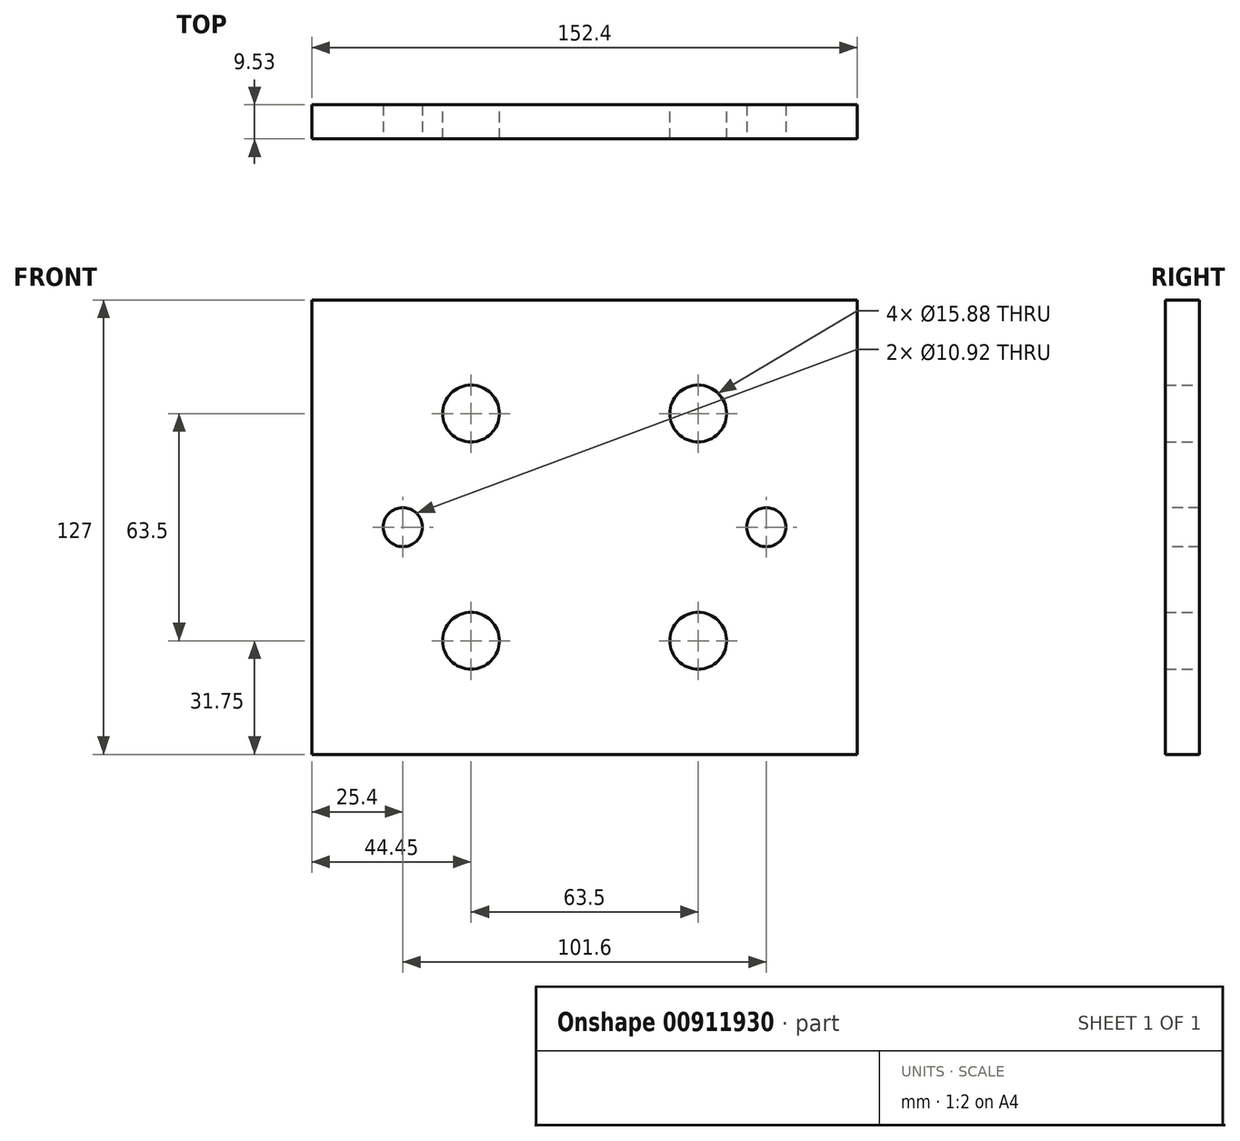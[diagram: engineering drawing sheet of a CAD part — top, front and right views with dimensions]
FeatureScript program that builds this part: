
annotation { "Feature Type Name" : "Feature", "Feature Type Description" : "" }
export const myFeature = defineFeature(function(context is Context, id is Id, definition is map)
    precondition{}
    {
        {
            var Q0;
            Q0=qCreatedBy(makeId("Front.planeOp"),FACE);
            var sketch = newSketch(context, id + "F0", { "sketchPlane" : qUnion([Q0])});
            skLineSegment(sketch, "E0.bottom", {"start": v(0, 0) * mm, "end": v(152.4, 0) * mm});
            skLineSegment(sketch, "E0.top", {"start": v(0, 127) * mm, "end": v(152.4, 127) * mm});
            skLineSegment(sketch, "E0.left", {"start": v(0, 0) * mm, "end": v(0, 127) * mm});
            skLineSegment(sketch, "E0.right", {"start": v(152.4, 0) * mm, "end": v(152.4, 127) * mm});
            skCircle(sketch, "E1", {"center": v(44.45, 31.75) * mm, "radius": 7.94 * mm});
            skCircle(sketch, "E2", {"center": v(107.95, 31.75) * mm, "radius": 7.94 * mm});
            skCircle(sketch, "E3", {"center": v(107.95, 95.25) * mm, "radius": 7.94 * mm});
            skCircle(sketch, "E4", {"center": v(44.45, 95.25) * mm, "radius": 7.94 * mm});
            skSolve(sketch);
        }
        {
            var Q0;
            Q0=makeQuery(id+"F0.imprint","IMPRINT",FACE,{"disambiguationData":[TD([[makeQuery(id+"F0.imprint","IMPRINT",EDGE,{"derivedFrom":sQuery(id+"F0.wireOp",EDGE,"E0.bottom")}),1.0]])]});
            extrude(context, id + "F1", {"entities" : qUnion([Q0]), "depth" : 9.52 * mm, "offsetDistance" : 25.4 * mm});
        }
        {
            var Q0;
            Q0=makeQuery(id+"F1.opExtrude","CAP_FACE",FACE,{"disambiguationData":[OSD([sQuery(id+"F0.wireOp",EDGE,"E0.bottom"),sQuery(id+"F0.wireOp",EDGE,"E0.top"),sQuery(id+"F0.wireOp",EDGE,"E0.left"),sQuery(id+"F0.wireOp",EDGE,"E0.right"),sQuery(id+"F0.wireOp",EDGE,"E1"),sQuery(id+"F0.wireOp",EDGE,"E2"),sQuery(id+"F0.wireOp",EDGE,"E3"),sQuery(id+"F0.wireOp",EDGE,"E4")])],"isStart":false});
            var sketch = newSketch(context, id + "F2", { "sketchPlane" : qUnion([Q0])});
            skCircle(sketch, "E5", {"center": v(25.4, 63.5) * mm, "radius": 5.46 * mm});
            skCircle(sketch, "E6", {"center": v(127, 63.5) * mm, "radius": 5.46 * mm});
            skSolve(sketch);
        }
        {
            var Q0;
            Q0=makeQuery(id+"F2.imprint","IMPRINT",FACE,{"disambiguationData":[TD([[makeQuery(id+"F2.imprint","IMPRINT",EDGE,{"derivedFrom":sQuery(id+"F2.wireOp",EDGE,"E5")}),1.0]])]});
            var Q1;
            Q1=makeQuery(id+"F2.imprint","IMPRINT",FACE,{"disambiguationData":[TD([[makeQuery(id+"F2.imprint","IMPRINT",EDGE,{"derivedFrom":sQuery(id+"F2.wireOp",EDGE,"E6")}),1.0]])]});
            extrude(context, id + "F3", {"entities" : qUnion([Q0, Q1]), "operationType" : NewBodyOperationType.REMOVE, "endBound" : BoundingType.THROUGH_ALL, "oppositeDirection" : true, "depth" : 25.4 * mm, "offsetDistance" : 25.4 * mm});
        }
    });
